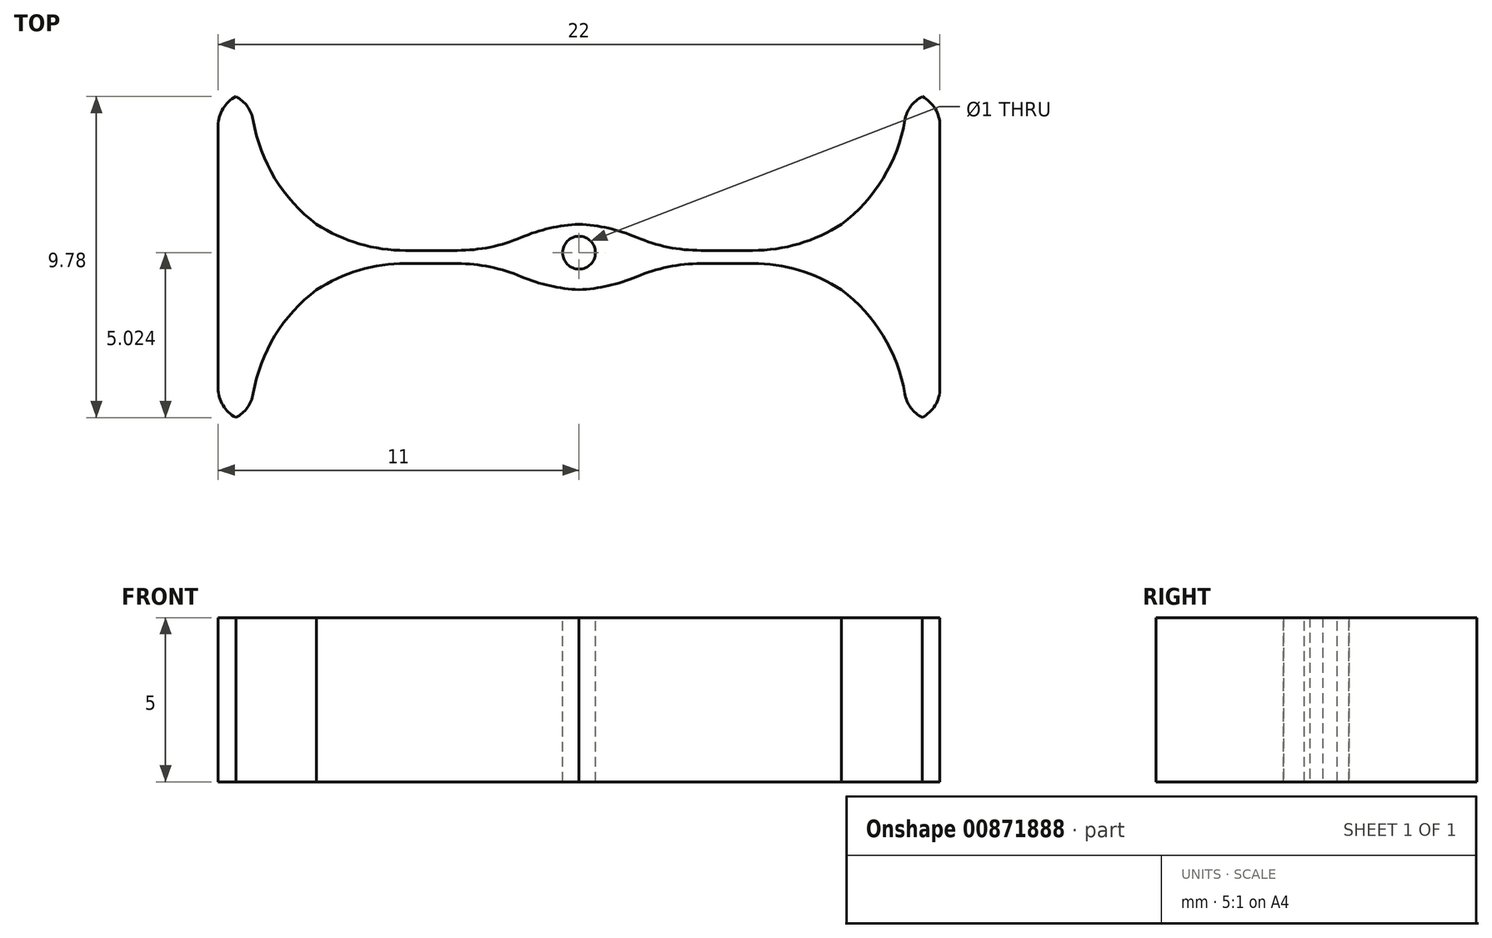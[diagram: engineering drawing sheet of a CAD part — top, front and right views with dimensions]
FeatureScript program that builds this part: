
annotation { "Feature Type Name" : "Feature", "Feature Type Description" : "" }
export const myFeature = defineFeature(function(context is Context, id is Id, definition is map)
    precondition{}
    {
        {
            var Q0;
            Q0=qCreatedBy(makeId("Top.planeOp"),FACE);
            var sketch = newSketch(context, id + "F0", { "sketchPlane" : qUnion([Q0])});
            skLineSegment(sketch, "E0.bottom", {"start": v(-1, 8.7) * mm, "end": v(0, 8.7) * mm});
            skLineSegment(sketch, "E0.top", {"start": v(-1, -1.3) * mm, "end": v(0, -1.3) * mm});
            skLineSegment(sketch, "E0.left", {"start": v(-1, 8.7) * mm, "end": v(-1, -1.3) * mm});
            skLineSegment(sketch, "E0.right", {"start": v(0, 8.7) * mm, "end": v(0, -1.3) * mm});
            skLineSegment(sketch, "E1.bottom", {"start": v(20, -1.3) * mm, "end": v(21, -1.3) * mm});
            skLineSegment(sketch, "E1.top", {"start": v(20, 8.7) * mm, "end": v(21, 8.7) * mm});
            skLineSegment(sketch, "E1.left", {"start": v(20, -1.3) * mm, "end": v(20, 8.7) * mm});
            skLineSegment(sketch, "E1.right", {"start": v(21, -1.3) * mm, "end": v(21, 8.7) * mm});
            skLineSegment(sketch, "E2.bottom", {"start": v(0, 2.7) * mm, "end": v(2, 2.7) * mm});
            skLineSegment(sketch, "E2.top", {"start": v(0, 4.7) * mm, "end": v(2, 4.7) * mm});
            skLineSegment(sketch, "E2.left", {"start": v(0, 2.7) * mm, "end": v(0, 4.7) * mm});
            skLineSegment(sketch, "E2.right", {"start": v(2, 2.7) * mm, "end": v(2, 4.7) * mm});
            skLineSegment(sketch, "E3.bottom", {"start": v(2, 3.5) * mm, "end": v(9, 3.5) * mm});
            skLineSegment(sketch, "E3.top", {"start": v(2, 3.9) * mm, "end": v(9, 3.9) * mm});
            skLineSegment(sketch, "E3.left", {"start": v(2, 3.5) * mm, "end": v(2, 3.9) * mm});
            skLineSegment(sketch, "E3.right", {"start": v(9, 3.5) * mm, "end": v(9, 3.9) * mm});
            skLineSegment(sketch, "E4.bottom", {"start": v(20, 2.7) * mm, "end": v(18, 2.7) * mm});
            skLineSegment(sketch, "E4.top", {"start": v(20, 4.7) * mm, "end": v(18, 4.7) * mm});
            skLineSegment(sketch, "E4.left", {"start": v(20, 2.7) * mm, "end": v(20, 4.7) * mm});
            skLineSegment(sketch, "E4.right", {"start": v(18, 2.7) * mm, "end": v(18, 4.7) * mm});
            skLineSegment(sketch, "E5.bottom", {"start": v(11, 3.9) * mm, "end": v(18, 3.9) * mm});
            skLineSegment(sketch, "E5.top", {"start": v(11, 3.5) * mm, "end": v(18, 3.5) * mm});
            skLineSegment(sketch, "E5.left", {"start": v(11, 3.9) * mm, "end": v(11, 3.5) * mm});
            skLineSegment(sketch, "E5.right", {"start": v(18, 3.9) * mm, "end": v(18, 3.5) * mm});
            skLineSegment(sketch, "E6.bottom", {"start": v(9, 4.7) * mm, "end": v(11, 4.7) * mm});
            skLineSegment(sketch, "E6.top", {"start": v(9, 2.7) * mm, "end": v(11, 2.7) * mm});
            skLineSegment(sketch, "E6.left", {"start": v(9, 4.7) * mm, "end": v(9, 2.7) * mm});
            skLineSegment(sketch, "E6.right", {"start": v(11, 4.7) * mm, "end": v(11, 2.7) * mm});
            skSolve(sketch);
        }
        {
            var Q0;
            {var subQ3=sQuery(id+"F0.wireOp",EDGE,"E6.bottom");Q0=makeQuery(id+"F0.imprint","IMPRINT",FACE,{"disambiguationData":[TD([[makeQuery(id+"F0.imprint","IMPRINT",EDGE,{"derivedFrom":subQ3}),-1.0]])]});}
            var Q1;
            {var subQ0=sQuery(id+"F0.wireOp",EDGE,"E3.bottom");Q1=makeQuery(id+"F0.imprint","IMPRINT",FACE,{"disambiguationData":[TD([[makeQuery(id+"F0.imprint","IMPRINT",EDGE,{"derivedFrom":subQ0}),1.0]])]});}
            var Q2;
            {var subQ1=sQuery(id+"F0.wireOp",EDGE,"E2.bottom");Q2=makeQuery(id+"F0.imprint","IMPRINT",FACE,{"disambiguationData":[TD([[makeQuery(id+"F0.imprint","IMPRINT",EDGE,{"derivedFrom":subQ1}),1.0]])]});}
            var Q3;
            {var subQ1=sQuery(id+"F0.wireOp",EDGE,"E0.bottom");Q3=makeQuery(id+"F0.imprint","IMPRINT",FACE,{"disambiguationData":[TD([[makeQuery(id+"F0.imprint","IMPRINT",EDGE,{"derivedFrom":subQ1}),-1.0]])]});}
            var Q4;
            {var subQ0=sQuery(id+"F0.wireOp",EDGE,"E5.bottom");Q4=makeQuery(id+"F0.imprint","IMPRINT",FACE,{"disambiguationData":[TD([[makeQuery(id+"F0.imprint","IMPRINT",EDGE,{"derivedFrom":subQ0}),-1.0]])]});}
            var Q5;
            {var subQ1=sQuery(id+"F0.wireOp",EDGE,"E4.bottom");Q5=makeQuery(id+"F0.imprint","IMPRINT",FACE,{"disambiguationData":[TD([[makeQuery(id+"F0.imprint","IMPRINT",EDGE,{"derivedFrom":subQ1}),-1.0]])]});}
            var Q6;
            {var subQ3=sQuery(id+"F0.wireOp",EDGE,"E1.bottom");Q6=makeQuery(id+"F0.imprint","IMPRINT",FACE,{"disambiguationData":[TD([[makeQuery(id+"F0.imprint","IMPRINT",EDGE,{"derivedFrom":subQ3}),1.0]])]});}
            extrude(context, id + "F1", {"entities" : qUnion([Q0, Q1, Q2, Q3, Q4, Q5, Q6]), "depth" : 5 * mm, "offsetDistance" : 25 * mm});
        }
        {
            var Q0;
            Q0=makeQuery(id+"F1.opExtrude","SWEPT_EDGE",EDGE,{"disambiguationData":[OSD([sQuery(id+"F0.wireOp",EDGE,"E3.bottom"),sQuery(id+"F0.wireOp",EDGE,"E6.left")])]});
            var Q1;
            Q1=makeQuery(id+"F1.opExtrude","SWEPT_EDGE",EDGE,{"disambiguationData":[OSD([sQuery(id+"F0.wireOp",EDGE,"E4.right"),sQuery(id+"F0.wireOp",EDGE,"E5.top"),sQuery(id+"F0.wireOp",EDGE,"E5.right")])]});
            var Q2;
            Q2=makeQuery(id+"F1.opExtrude","SWEPT_EDGE",EDGE,{"disambiguationData":[OSD([sQuery(id+"F0.wireOp",EDGE,"E2.right"),sQuery(id+"F0.wireOp",EDGE,"E3.bottom"),sQuery(id+"F0.wireOp",EDGE,"E3.left")])]});
            var Q3;
            Q3=makeQuery(id+"F1.opExtrude","SWEPT_EDGE",EDGE,{"disambiguationData":[OSD([sQuery(id+"F0.wireOp",EDGE,"E5.top"),sQuery(id+"F0.wireOp",EDGE,"E6.right")])]});
            var Q4;
            Q4=makeQuery(id+"F1.opExtrude","SWEPT_EDGE",EDGE,{"disambiguationData":[OSD([sQuery(id+"F0.wireOp",EDGE,"E5.bottom"),sQuery(id+"F0.wireOp",EDGE,"E6.right")])]});
            var Q5;
            Q5=makeQuery(id+"F1.opExtrude","SWEPT_EDGE",EDGE,{"disambiguationData":[OSD([sQuery(id+"F0.wireOp",EDGE,"E2.right"),sQuery(id+"F0.wireOp",EDGE,"E3.top"),sQuery(id+"F0.wireOp",EDGE,"E3.left")])]});
            var Q6;
            Q6=makeQuery(id+"F1.opExtrude","SWEPT_EDGE",EDGE,{"disambiguationData":[OSD([sQuery(id+"F0.wireOp",EDGE,"E3.top"),sQuery(id+"F0.wireOp",EDGE,"E6.left")])]});
            var Q7;
            Q7=makeQuery(id+"F1.opExtrude","SWEPT_EDGE",EDGE,{"disambiguationData":[OSD([sQuery(id+"F0.wireOp",EDGE,"E4.right"),sQuery(id+"F0.wireOp",EDGE,"E5.bottom"),sQuery(id+"F0.wireOp",EDGE,"E5.right")])]});
            fillet(context, id + "F2", {"entities" : qUnion([Q0, Q1, Q2, Q3, Q4, Q5, Q6, Q7]), "radius" : 5 * mm, "tangentPropagation" : true, "allowEdgeOverflow" : false});
        }
        {
            var Q0;
            Q0=makeQuery(id+"F1.opExtrude","SWEPT_EDGE",EDGE,{"disambiguationData":[OSD([sQuery(id+"F0.wireOp",EDGE,"E1.left"),sQuery(id+"F0.wireOp",EDGE,"E4.top"),sQuery(id+"F0.wireOp",EDGE,"E4.left")])]});
            var Q1;
            Q1=makeQuery(id+"F1.opExtrude","SWEPT_EDGE",EDGE,{"disambiguationData":[OSD([sQuery(id+"F0.wireOp",EDGE,"E0.right"),sQuery(id+"F0.wireOp",EDGE,"E2.top"),sQuery(id+"F0.wireOp",EDGE,"E2.left")])]});
            var Q2;
            Q2=makeQuery(id+"F1.opExtrude","SWEPT_EDGE",EDGE,{"disambiguationData":[OSD([sQuery(id+"F0.wireOp",EDGE,"E0.right"),sQuery(id+"F0.wireOp",EDGE,"E2.bottom"),sQuery(id+"F0.wireOp",EDGE,"E2.left")])]});
            var Q3;
            Q3=makeQuery(id+"F1.opExtrude","SWEPT_EDGE",EDGE,{"disambiguationData":[OSD([sQuery(id+"F0.wireOp",EDGE,"E1.left"),sQuery(id+"F0.wireOp",EDGE,"E4.bottom"),sQuery(id+"F0.wireOp",EDGE,"E4.left")])]});
            fillet(context, id + "F3", {"entities" : qUnion([Q0, Q1, Q2, Q3]), "radius" : 5 * mm, "tangentPropagation" : true, "allowEdgeOverflow" : false});
        }
        {
            var Q0;
            Q0=makeQuery(id+"F2.opFillet","BLEND_EDGE",EDGE,{"blendedFrom":[makeQuery(id+"F1.opExtrude","SWEPT_EDGE",EDGE,{"disambiguationData":[OSD([sQuery(id+"F0.wireOp",EDGE,"E5.bottom"),sQuery(id+"F0.wireOp",EDGE,"E6.right")])]}),makeQuery(id+"F1.opExtrude","SWEPT_FACE",FACE,{"disambiguationData":[OSD([sQuery(id+"F0.wireOp",EDGE,"E6.bottom")])]})],"blendedInto":[makeQuery(id+"F1.opExtrude","SWEPT_FACE",FACE,{"disambiguationData":[OSD([sQuery(id+"F0.wireOp",EDGE,"E6.bottom")])]})]});
            var Q1;
            Q1=makeQuery(id+"F2.opFillet","BLEND_EDGE",EDGE,{"blendedFrom":[makeQuery(id+"F1.opExtrude","SWEPT_EDGE",EDGE,{"disambiguationData":[OSD([sQuery(id+"F0.wireOp",EDGE,"E3.top"),sQuery(id+"F0.wireOp",EDGE,"E6.left")])]}),makeQuery(id+"F1.opExtrude","SWEPT_FACE",FACE,{"disambiguationData":[OSD([sQuery(id+"F0.wireOp",EDGE,"E6.bottom")])]})],"blendedInto":[makeQuery(id+"F1.opExtrude","SWEPT_FACE",FACE,{"disambiguationData":[OSD([sQuery(id+"F0.wireOp",EDGE,"E6.bottom")])]})]});
            var Q2;
            Q2=makeQuery(id+"F2.opFillet","BLEND_EDGE",EDGE,{"blendedFrom":[makeQuery(id+"F1.opExtrude","SWEPT_EDGE",EDGE,{"disambiguationData":[OSD([sQuery(id+"F0.wireOp",EDGE,"E5.top"),sQuery(id+"F0.wireOp",EDGE,"E6.right")])]}),makeQuery(id+"F1.opExtrude","SWEPT_FACE",FACE,{"disambiguationData":[OSD([sQuery(id+"F0.wireOp",EDGE,"E6.top")])]})],"blendedInto":[makeQuery(id+"F1.opExtrude","SWEPT_FACE",FACE,{"disambiguationData":[OSD([sQuery(id+"F0.wireOp",EDGE,"E6.top")])]})]});
            var Q3;
            Q3=makeQuery(id+"F2.opFillet","BLEND_EDGE",EDGE,{"blendedFrom":[makeQuery(id+"F1.opExtrude","SWEPT_EDGE",EDGE,{"disambiguationData":[OSD([sQuery(id+"F0.wireOp",EDGE,"E3.bottom"),sQuery(id+"F0.wireOp",EDGE,"E6.left")])]}),makeQuery(id+"F1.opExtrude","SWEPT_FACE",FACE,{"disambiguationData":[OSD([sQuery(id+"F0.wireOp",EDGE,"E6.top")])]})],"blendedInto":[makeQuery(id+"F1.opExtrude","SWEPT_FACE",FACE,{"disambiguationData":[OSD([sQuery(id+"F0.wireOp",EDGE,"E6.top")])]})]});
            fillet(context, id + "F4", {"entities" : qUnion([Q0, Q1, Q2, Q3]), "radius" : 5 * mm, "tangentPropagation" : true, "allowEdgeOverflow" : false});
        }
        {
            var Q0;
            Q0=makeQuery(id+"F3.opFillet","BLEND_EDGE",EDGE,{"blendedFrom":[makeQuery(id+"F1.opExtrude","SWEPT_EDGE",EDGE,{"disambiguationData":[OSD([sQuery(id+"F0.wireOp",EDGE,"E1.left"),sQuery(id+"F0.wireOp",EDGE,"E4.top"),sQuery(id+"F0.wireOp",EDGE,"E4.left")])]}),makeQuery(id+"F1.opExtrude","SWEPT_FACE",FACE,{"disambiguationData":[OSD([sQuery(id+"F0.wireOp",EDGE,"E1.top")])]})],"blendedInto":[makeQuery(id+"F1.opExtrude","SWEPT_FACE",FACE,{"disambiguationData":[OSD([sQuery(id+"F0.wireOp",EDGE,"E1.top")])]})]});
            var Q1;
            Q1=makeQuery(id+"F1.opExtrude","SWEPT_EDGE",EDGE,{"disambiguationData":[OSD([sQuery(id+"F0.wireOp",EDGE,"E1.top"),sQuery(id+"F0.wireOp",EDGE,"E1.right")])]});
            var Q2;
            Q2=makeQuery(id+"F1.opExtrude","SWEPT_EDGE",EDGE,{"disambiguationData":[OSD([sQuery(id+"F0.wireOp",EDGE,"E1.bottom"),sQuery(id+"F0.wireOp",EDGE,"E1.right")])]});
            var Q3;
            Q3=makeQuery(id+"F3.opFillet","BLEND_EDGE",EDGE,{"blendedFrom":[makeQuery(id+"F1.opExtrude","SWEPT_EDGE",EDGE,{"disambiguationData":[OSD([sQuery(id+"F0.wireOp",EDGE,"E1.left"),sQuery(id+"F0.wireOp",EDGE,"E4.bottom"),sQuery(id+"F0.wireOp",EDGE,"E4.left")])]}),makeQuery(id+"F1.opExtrude","SWEPT_FACE",FACE,{"disambiguationData":[OSD([sQuery(id+"F0.wireOp",EDGE,"E1.bottom")])]})],"blendedInto":[makeQuery(id+"F1.opExtrude","SWEPT_FACE",FACE,{"disambiguationData":[OSD([sQuery(id+"F0.wireOp",EDGE,"E1.bottom")])]})]});
            var Q4;
            Q4=makeQuery(id+"F1.opExtrude","SWEPT_EDGE",EDGE,{"disambiguationData":[OSD([sQuery(id+"F0.wireOp",EDGE,"E0.bottom"),sQuery(id+"F0.wireOp",EDGE,"E0.left")])]});
            var Q5;
            Q5=makeQuery(id+"F3.opFillet","BLEND_EDGE",EDGE,{"blendedFrom":[makeQuery(id+"F1.opExtrude","SWEPT_EDGE",EDGE,{"disambiguationData":[OSD([sQuery(id+"F0.wireOp",EDGE,"E0.right"),sQuery(id+"F0.wireOp",EDGE,"E2.top"),sQuery(id+"F0.wireOp",EDGE,"E2.left")])]}),makeQuery(id+"F1.opExtrude","SWEPT_FACE",FACE,{"disambiguationData":[OSD([sQuery(id+"F0.wireOp",EDGE,"E0.bottom")])]})],"blendedInto":[makeQuery(id+"F1.opExtrude","SWEPT_FACE",FACE,{"disambiguationData":[OSD([sQuery(id+"F0.wireOp",EDGE,"E0.bottom")])]})]});
            var Q6;
            Q6=makeQuery(id+"F3.opFillet","BLEND_EDGE",EDGE,{"blendedFrom":[makeQuery(id+"F1.opExtrude","SWEPT_EDGE",EDGE,{"disambiguationData":[OSD([sQuery(id+"F0.wireOp",EDGE,"E0.right"),sQuery(id+"F0.wireOp",EDGE,"E2.bottom"),sQuery(id+"F0.wireOp",EDGE,"E2.left")])]}),makeQuery(id+"F1.opExtrude","SWEPT_FACE",FACE,{"disambiguationData":[OSD([sQuery(id+"F0.wireOp",EDGE,"E0.top")])]})],"blendedInto":[makeQuery(id+"F1.opExtrude","SWEPT_FACE",FACE,{"disambiguationData":[OSD([sQuery(id+"F0.wireOp",EDGE,"E0.top")])]})]});
            var Q7;
            Q7=makeQuery(id+"F1.opExtrude","SWEPT_EDGE",EDGE,{"disambiguationData":[OSD([sQuery(id+"F0.wireOp",EDGE,"E0.top"),sQuery(id+"F0.wireOp",EDGE,"E0.left")])]});
            fillet(context, id + "F5", {"entities" : qUnion([Q0, Q1, Q2, Q3, Q4, Q5, Q6, Q7]), "radius" : 1 * mm, "tangentPropagation" : true, "allowEdgeOverflow" : false});
        }
        {
            var Q0;
            Q0=makeQuery(id+"F1.opExtrude","CAP_FACE",FACE,{"disambiguationData":[OSD([sQuery(id+"F0.wireOp",EDGE,"E0.bottom"),sQuery(id+"F0.wireOp",EDGE,"E0.top"),sQuery(id+"F0.wireOp",EDGE,"E0.left"),sQuery(id+"F0.wireOp",EDGE,"E0.right"),sQuery(id+"F0.wireOp",EDGE,"E1.bottom"),sQuery(id+"F0.wireOp",EDGE,"E1.top"),sQuery(id+"F0.wireOp",EDGE,"E1.left"),sQuery(id+"F0.wireOp",EDGE,"E1.right"),sQuery(id+"F0.wireOp",EDGE,"E2.bottom"),sQuery(id+"F0.wireOp",EDGE,"E2.top"),sQuery(id+"F0.wireOp",EDGE,"E2.right"),sQuery(id+"F0.wireOp",EDGE,"E3.bottom"),sQuery(id+"F0.wireOp",EDGE,"E3.top"),sQuery(id+"F0.wireOp",EDGE,"E4.bottom"),sQuery(id+"F0.wireOp",EDGE,"E4.top"),sQuery(id+"F0.wireOp",EDGE,"E4.right"),sQuery(id+"F0.wireOp",EDGE,"E5.bottom"),sQuery(id+"F0.wireOp",EDGE,"E5.top"),sQuery(id+"F0.wireOp",EDGE,"E6.bottom"),sQuery(id+"F0.wireOp",EDGE,"E6.top"),sQuery(id+"F0.wireOp",EDGE,"E6.left"),sQuery(id+"F0.wireOp",EDGE,"E6.right")])],"isStart":false});
            var sketch = newSketch(context, id + "F6", { "sketchPlane" : qUnion([Q0])});
            skCircle(sketch, "E7", {"center": v(10, 3.83) * mm, "radius": 0.5 * mm});
            skLineSegment(sketch, "E8", {"start": v(10, 4.7) * mm, "end": v(10, 2.7) * mm, "construction": true});
            skLineSegment(sketch, "E9", {"start": v(21, 3.7) * mm, "end": v(-1, 4) * mm, "construction": true});
            skSolve(sketch);
        }
        {
            var Q0;
            Q0 = qSketchRegion(id + "F6", true);
            extrude(context, id + "F7", {"entities" : qUnion([Q0]), "operationType" : NewBodyOperationType.REMOVE, "endBound" : BoundingType.THROUGH_ALL, "oppositeDirection" : true, "depth" : 25 * mm, "offsetDistance" : 25 * mm});
        }
    });
